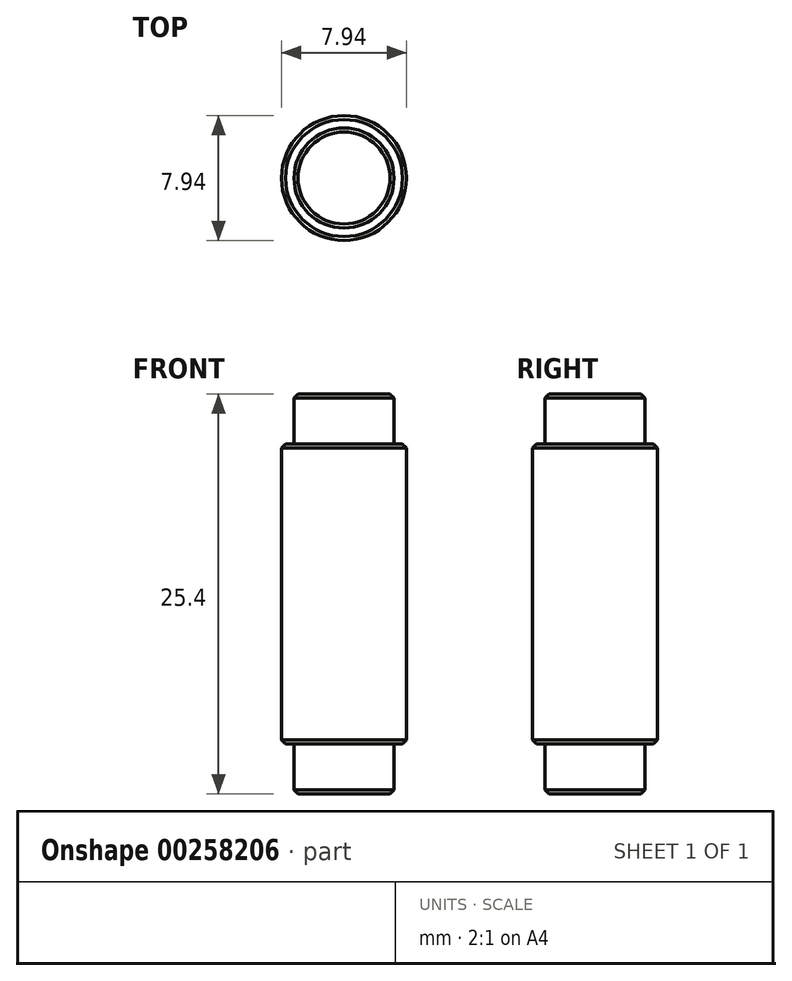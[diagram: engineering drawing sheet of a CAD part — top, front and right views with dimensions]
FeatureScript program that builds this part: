
annotation { "Feature Type Name" : "Feature", "Feature Type Description" : "" }
export const myFeature = defineFeature(function(context is Context, id is Id, definition is map)
    precondition{}
    {
        {
            var Q0;
            Q0=qCreatedBy(makeId("Top.planeOp"),FACE);
            var sketch = newSketch(context, id + "F0", { "sketchPlane" : qUnion([Q0])});
            skCircle(sketch, "E0", {"center": v(0, 0) * mm, "radius": 3.97 * mm});
            skSolve(sketch);
        }
        {
            var Q0;
            Q0 = qSketchRegion(id + "F0", true);
            extrude(context, id + "F1", {"entities" : qUnion([Q0]), "depth" : 9.52 * mm});
        }
        {
            var Q0;
            Q0=makeQuery(id+"F1.opExtrude","CAP_FACE",FACE,{"disambiguationData":[OSD([sQuery(id+"F0.wireOp",EDGE,"E0")])],"isStart":false});
            var sketch = newSketch(context, id + "F2", { "sketchPlane" : qUnion([Q0])});
            skCircle(sketch, "E1", {"center": v(0, 0) * mm, "radius": 3.18 * mm});
            skSolve(sketch);
        }
        {
            var Q0;
            Q0 = qSketchRegion(id + "F2", true);
            extrude(context, id + "F3", {"entities" : qUnion([Q0]), "operationType" : NewBodyOperationType.ADD, "depth" : 3.17 * mm});
        }
        {
            var Q0;
            Q0=makeQuery(id+"F1.opExtrude","CAP_FACE",FACE,{"disambiguationData":[OSD([sQuery(id+"F0.wireOp",EDGE,"E0")])],"isStart":true});
            var sketch = newSketch(context, id + "F4", { "sketchPlane" : qUnion([Q0])});
            skSolve(sketch);
        }
        {
            var Q0;
            Q0=makeQuery(id+"F4.imprint","IMPRINT",FACE,{"disambiguationData":[TD([[makeQuery(id+"F4.imprint","IMPRINT",EDGE,{"derivedFrom":makeQuery(id+"F1.opExtrude","CAP_EDGE",EDGE,{"disambiguationData":[OSD([sQuery(id+"F0.wireOp",EDGE,"E0")])],"isStart":true})}),-1.0]])]});
            extrude(context, id + "F5", {"entities" : qUnion([Q0]), "operationType" : NewBodyOperationType.ADD, "depth" : 9.52 * mm});
        }
        {
            var Q0;
            Q0=makeQuery(id+"F5.opExtrude","CAP_FACE",FACE,{"disambiguationData":[OSD([sQuery(id+"F0.wireOp",EDGE,"E0")])],"isStart":false});
            var sketch = newSketch(context, id + "F6", { "sketchPlane" : qUnion([Q0])});
            skCircle(sketch, "E2", {"center": v(0, 0) * mm, "radius": 3.18 * mm});
            skSolve(sketch);
        }
        {
            var Q0;
            Q0 = qSketchRegion(id + "F6", true);
            extrude(context, id + "F7", {"entities" : qUnion([Q0]), "operationType" : NewBodyOperationType.ADD, "depth" : 3.17 * mm});
        }
        {
            var Q0;
            Q0=makeQuery(id+"F3.opExtrude","CAP_EDGE",EDGE,{"disambiguationData":[OSD([sQuery(id+"F2.wireOp",EDGE,"E1")])],"isStart":false});
            var Q1;
            Q1=makeQuery(id+"F1.opExtrude","CAP_EDGE",EDGE,{"disambiguationData":[OSD([sQuery(id+"F0.wireOp",EDGE,"E0")])],"isStart":false});
            var Q2;
            Q2=makeQuery(id+"F5.opExtrude","CAP_EDGE",EDGE,{"disambiguationData":[OSD([sQuery(id+"F0.wireOp",EDGE,"E0")])],"isStart":false});
            var Q3;
            Q3=makeQuery(id+"F7.opExtrude","CAP_EDGE",EDGE,{"disambiguationData":[OSD([sQuery(id+"F6.wireOp",EDGE,"E2")])],"isStart":false});
            chamfer(context, id + "F8", {"entities" : qUnion([Q0, Q1, Q2, Q3]), "width" : 0.25 * mm, "tangentPropagation" : true});
        }
    });
